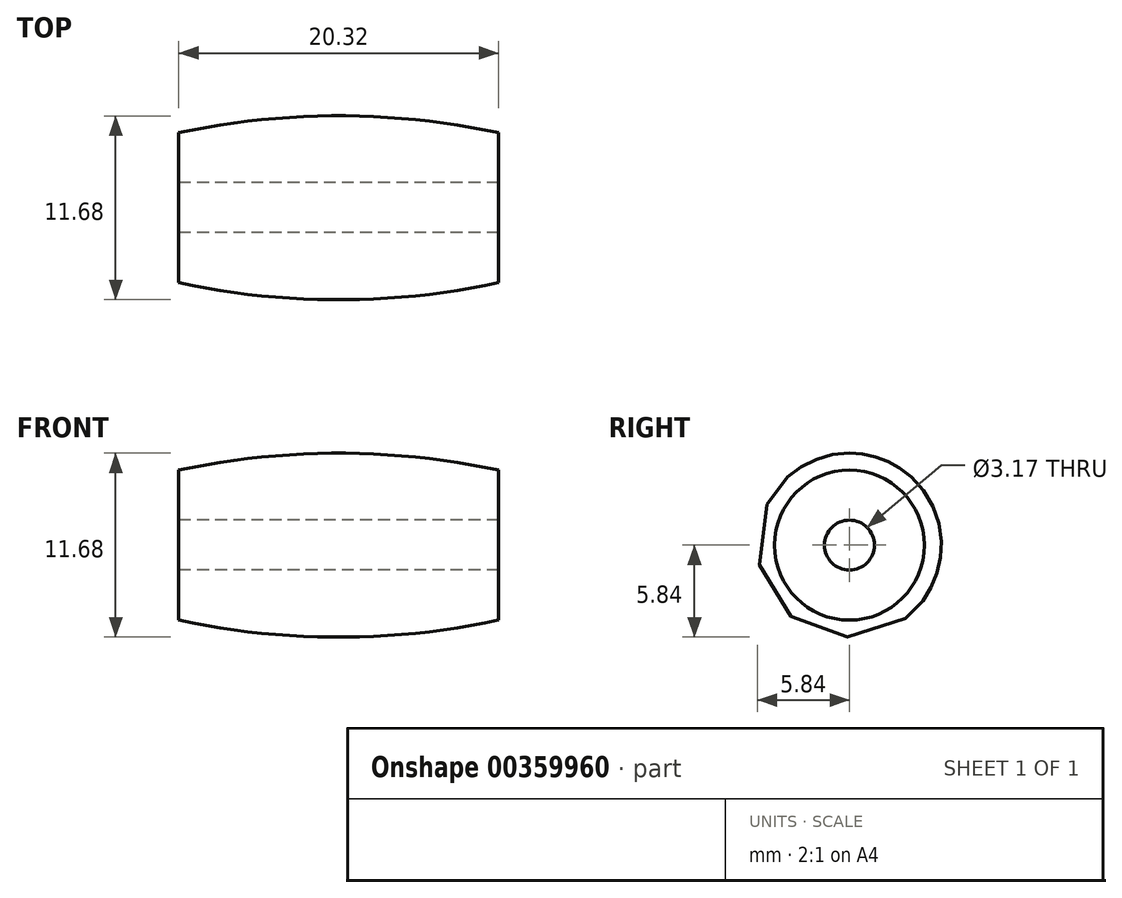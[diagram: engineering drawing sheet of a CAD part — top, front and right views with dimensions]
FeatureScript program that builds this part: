
annotation { "Feature Type Name" : "Feature", "Feature Type Description" : "" }
export const myFeature = defineFeature(function(context is Context, id is Id, definition is map)
    precondition{}
    {
        {
            var Q0;
            Q0=qCreatedBy(makeId("Front.planeOp"),FACE);
            var sketch = newSketch(context, id + "F0", { "sketchPlane" : qUnion([Q0])});
            skLineSegment(sketch, "E0", {"start": v(-10.16, 4.76) * mm, "end": v(-10.16, 1.59) * mm});
            skLineSegment(sketch, "E1", {"start": v(-10.16, 1.59) * mm, "end": v(10.16, 1.59) * mm});
            skLineSegment(sketch, "E2", {"start": v(10.16, 1.59) * mm, "end": v(10.16, 4.76) * mm});
            skArc(sketch, "E3", {"start": v(10.16, 4.76) * mm, "mid": v(0, 5.84) * mm, "end": v(-10.16, 4.76) * mm});
            skLineSegment(sketch, "E4", {"start": v(-44.5, 0) * mm, "end": v(44.5, 0) * mm, "construction": true});
            skPoint(sketch, "E5", {"position": v(0, 1.59) * mm});
            skSolve(sketch);
        }
        {
            var Q0;
            Q0 = qSketchRegion(id + "F0", true);
            var Q1;
            Q1=sQuery(id+"F0.wireOp",EDGE,"E4");
            revolve(context, id + "F1", {"entities" : qUnion([Q0]), "axis" : qUnion([Q1]), "revolveType" : RevolveType.FULL});
        }
    });
